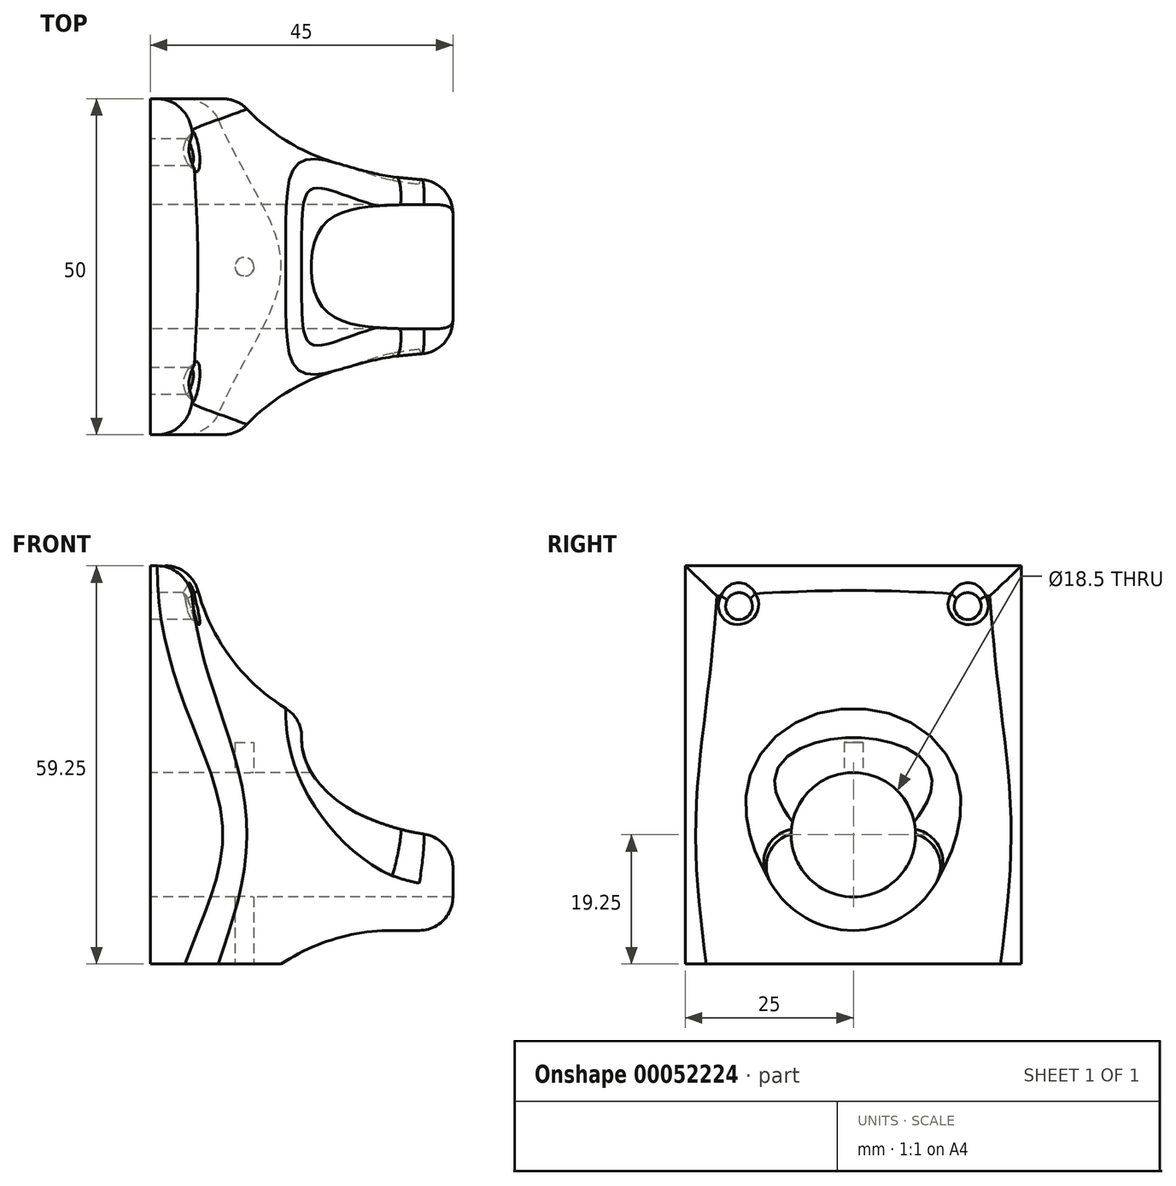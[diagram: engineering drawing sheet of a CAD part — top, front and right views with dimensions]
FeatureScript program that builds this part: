
annotation { "Feature Type Name" : "Feature", "Feature Type Description" : "" }
export const myFeature = defineFeature(function(context is Context, id is Id, definition is map)
    precondition{}
    {
        {
            var Q0;
            Q0=qCreatedBy(makeId("Right.planeOp"),FACE);
            var sketch = newSketch(context, id + "F0", { "sketchPlane" : qUnion([Q0])});
            skLineSegment(sketch, "E0.bottom", {"start": v(-25, 40) * mm, "end": v(25, 40) * mm});
            skLineSegment(sketch, "E0.top", {"start": v(-25, -19.25) * mm, "end": v(25, -19.25) * mm});
            skLineSegment(sketch, "E0.left", {"start": v(-25, 40) * mm, "end": v(-25, -19.25) * mm});
            skLineSegment(sketch, "E0.right", {"start": v(25, 40) * mm, "end": v(25, -19.25) * mm});
            skCircle(sketch, "E1", {"center": v(0, 0) * mm, "radius": 9.25 * mm});
            skCircle(sketch, "E2", {"center": v(0, 0) * mm, "radius": 14.25 * mm});
            skLineSegment(sketch, "E3", {"start": v(0, 40) * mm, "end": v(0, -19.25) * mm, "construction": true});
            skCircle(sketch, "E4", {"center": v(-17, 34) * mm, "radius": 2 * mm});
            skCircle(sketch, "E5.MirrorC", {"center": v(17, 34) * mm, "radius": 2 * mm});
            skSolve(sketch);
        }
        {
            var Q0;
            Q0=makeQuery(id+"F0.imprint","IMPRINT",FACE,{"disambiguationData":[TD([[makeQuery(id+"F0.imprint","IMPRINT",EDGE,{"derivedFrom":sQuery(id+"F0.wireOp",EDGE,"E0.bottom")}),-1.0]])]});
            var Q1;
            Q1=makeQuery(id+"F0.imprint","IMPRINT",FACE,{"disambiguationData":[TD([[makeQuery(id+"F0.imprint","IMPRINT",EDGE,{"derivedFrom":sQuery(id+"F0.wireOp",EDGE,"E1")}),-1.0]])]});
            extrude(context, id + "F1", {"entities" : qUnion([Q0, Q1]), "depth" : 6 * mm});
        }
        {
            var Q0;
            Q0=makeQuery(id+"F0.imprint","IMPRINT",FACE,{"disambiguationData":[TD([[makeQuery(id+"F0.imprint","IMPRINT",EDGE,{"derivedFrom":sQuery(id+"F0.wireOp",EDGE,"E1")}),-1.0]])]});
            extrude(context, id + "F2", {"entities" : qUnion([Q0]), "operationType" : NewBodyOperationType.ADD, "depth" : 45 * mm});
        }
        {
            var Q0;
            Q0=qCreatedBy(makeId("Front.planeOp"),FACE);
            var sketch = newSketch(context, id + "F3", { "sketchPlane" : qUnion([Q0])});
            skLineSegment(sketch, "E6.0", {"start": v(45, 14.25) * mm, "end": v(45, -14.25) * mm, "construction": true});
            skEllipse(sketch, "E7", {"center": v(45, 14.25) * mm, "majorRadius": 22.5 * mm, "minorRadius": 14.25 * mm, "majorAxis": v(-1, 0)});
            skLineSegment(sketch, "E8", {"start": v(45, 14.25) * mm, "end": v(0, 14.25) * mm, "construction": true});
            skLineSegment(sketch, "E9", {"start": v(0, 0) * mm, "end": v(45, 0) * mm, "construction": true});
            skLineSegment(sketch, "E10", {"start": v(22.5, 0) * mm, "end": v(22.5, 14.25) * mm, "construction": true});
            skSolve(sketch);
        }
        {
            var Q0;
            Q0 = qSketchRegion(id + "F3", true);
            extrude(context, id + "F4", {"entities" : qUnion([Q0]), "operationType" : NewBodyOperationType.REMOVE, "endBound" : BoundingType.THROUGH_ALL, "oppositeDirection" : true, "depth" : 25 * mm, "hasSecondDirection" : true, "secondDirectionBound" : SecondDirectionBoundingType.THROUGH_ALL, "secondDirectionOppositeDirection" : false, "secondDirectionDepth" : 25 * mm});
        }
        {
            var Q0;
            Q0=makeQuery(id+"F2.boolean.opBoolean","INTERSECT",EDGE,{"derivedFrom":[makeQuery(id+"F1.opExtrude","CAP_FACE",FACE,{"disambiguationData":[OSD([sQuery(id+"F0.wireOp",EDGE,"E0.bottom"),sQuery(id+"F0.wireOp",EDGE,"E0.top"),sQuery(id+"F0.wireOp",EDGE,"E0.left"),sQuery(id+"F0.wireOp",EDGE,"E0.right"),sQuery(id+"F0.wireOp",EDGE,"E1"),sQuery(id+"F0.wireOp",EDGE,"E4"),sQuery(id+"F0.wireOp",EDGE,"E5.MirrorC")])],"isStart":false}),makeQuery(id+"F2.opExtrude","SWEPT_FACE",FACE,{"disambiguationData":[OSD([sQuery(id+"F0.wireOp",EDGE,"E2")])]})]});
            fillet(context, id + "F5", {"entities" : qUnion([Q0]), "radius" : 30 * mm, "tangentPropagation" : true, "allowEdgeOverflow" : false});
        }
        {
            var Q0;
            {var subQ0=sQuery(id+"F0.wireOp",EDGE,"E0.right");Q0=makeQuery(id+"F5.opFillet","BLEND_EDGE",EDGE,{"blendedFrom":[makeQuery(id+"F2.boolean.opBoolean","INTERSECT",EDGE,{"derivedFrom":[makeQuery(id+"F1.opExtrude","CAP_FACE",FACE,{"disambiguationData":[OSD([sQuery(id+"F0.wireOp",EDGE,"E0.bottom"),sQuery(id+"F0.wireOp",EDGE,"E0.top"),sQuery(id+"F0.wireOp",EDGE,"E0.left"),subQ0,sQuery(id+"F0.wireOp",EDGE,"E1"),sQuery(id+"F0.wireOp",EDGE,"E4"),sQuery(id+"F0.wireOp",EDGE,"E5.MirrorC")])],"isStart":false}),makeQuery(id+"F2.opExtrude","SWEPT_FACE",FACE,{"disambiguationData":[OSD([sQuery(id+"F0.wireOp",EDGE,"E2")])]})]}),makeQuery(id+"F1.opExtrude","SWEPT_FACE",FACE,{"disambiguationData":[OSD([subQ0])]})],"blendedInto":[makeQuery(id+"F1.opExtrude","SWEPT_FACE",FACE,{"disambiguationData":[OSD([subQ0])]})]});}
            var Q1;
            {var subQ0=sQuery(id+"F0.wireOp",EDGE,"E0.bottom");Q1=makeQuery(id+"F5.opFillet","BLEND_EDGE",EDGE,{"blendedFrom":[makeQuery(id+"F2.boolean.opBoolean","INTERSECT",EDGE,{"derivedFrom":[makeQuery(id+"F1.opExtrude","CAP_FACE",FACE,{"disambiguationData":[OSD([subQ0,sQuery(id+"F0.wireOp",EDGE,"E0.top"),sQuery(id+"F0.wireOp",EDGE,"E0.left"),sQuery(id+"F0.wireOp",EDGE,"E0.right"),sQuery(id+"F0.wireOp",EDGE,"E1"),sQuery(id+"F0.wireOp",EDGE,"E4"),sQuery(id+"F0.wireOp",EDGE,"E5.MirrorC")])],"isStart":false}),makeQuery(id+"F2.opExtrude","SWEPT_FACE",FACE,{"disambiguationData":[OSD([sQuery(id+"F0.wireOp",EDGE,"E2")])]})]}),makeQuery(id+"F1.opExtrude","SWEPT_FACE",FACE,{"disambiguationData":[OSD([subQ0])]})],"blendedInto":[makeQuery(id+"F1.opExtrude","SWEPT_FACE",FACE,{"disambiguationData":[OSD([subQ0])]})]});}
            var Q2;
            {var subQ0=sQuery(id+"F0.wireOp",EDGE,"E0.left");Q2=makeQuery(id+"F5.opFillet","BLEND_EDGE",EDGE,{"blendedFrom":[makeQuery(id+"F2.boolean.opBoolean","INTERSECT",EDGE,{"derivedFrom":[makeQuery(id+"F1.opExtrude","CAP_FACE",FACE,{"disambiguationData":[OSD([sQuery(id+"F0.wireOp",EDGE,"E0.bottom"),sQuery(id+"F0.wireOp",EDGE,"E0.top"),subQ0,sQuery(id+"F0.wireOp",EDGE,"E0.right"),sQuery(id+"F0.wireOp",EDGE,"E1"),sQuery(id+"F0.wireOp",EDGE,"E4"),sQuery(id+"F0.wireOp",EDGE,"E5.MirrorC")])],"isStart":false}),makeQuery(id+"F2.opExtrude","SWEPT_FACE",FACE,{"disambiguationData":[OSD([sQuery(id+"F0.wireOp",EDGE,"E2")])]})]}),makeQuery(id+"F1.opExtrude","SWEPT_FACE",FACE,{"disambiguationData":[OSD([subQ0])]})],"blendedInto":[makeQuery(id+"F1.opExtrude","SWEPT_FACE",FACE,{"disambiguationData":[OSD([subQ0])]})]});}
            fillet(context, id + "F6", {"entities" : qUnion([Q0, Q1, Q2]), "radius" : 5 * mm, "tangentPropagation" : true, "allowEdgeOverflow" : false});
        }
        {
            var Q0;
            Q0=makeQuery(id+"F5.opFillet","BLEND_EDGE",EDGE,{"blendedFrom":[makeQuery(id+"F2.boolean.opBoolean","INTERSECT",EDGE,{"derivedFrom":[makeQuery(id+"F1.opExtrude","CAP_FACE",FACE,{"disambiguationData":[OSD([sQuery(id+"F0.wireOp",EDGE,"E0.bottom"),sQuery(id+"F0.wireOp",EDGE,"E0.top"),sQuery(id+"F0.wireOp",EDGE,"E0.left"),sQuery(id+"F0.wireOp",EDGE,"E0.right"),sQuery(id+"F0.wireOp",EDGE,"E1"),sQuery(id+"F0.wireOp",EDGE,"E4"),sQuery(id+"F0.wireOp",EDGE,"E5.MirrorC")])],"isStart":false}),makeQuery(id+"F2.opExtrude","SWEPT_FACE",FACE,{"disambiguationData":[OSD([sQuery(id+"F0.wireOp",EDGE,"E2")])]})]}),makeQuery(id+"F4.boolean.opBoolean","COPY",FACE,{"derivedFrom":makeQuery(id+"F4.opExtrude","SWEPT_FACE",FACE,{"disambiguationData":[OSD([sQuery(id+"F3.wireOp",EDGE,"E7")])]})})],"blendedInto":[makeQuery(id+"F4.boolean.opBoolean","COPY",FACE,{"derivedFrom":makeQuery(id+"F4.opExtrude","SWEPT_FACE",FACE,{"disambiguationData":[OSD([sQuery(id+"F3.wireOp",EDGE,"E7")])]})})]});
            fillet(context, id + "F7", {"entities" : qUnion([Q0]), "radius" : 5 * mm, "tangentPropagation" : true, "allowEdgeOverflow" : false});
        }
        {
            var Q0;
            Q0=makeQuery(id+"F2.opExtrude","CAP_EDGE",EDGE,{"disambiguationData":[OSD([sQuery(id+"F0.wireOp",EDGE,"E2")])],"isStart":false});
            fillet(context, id + "F8", {"entities" : qUnion([Q0]), "radius" : 5 * mm, "tangentPropagation" : true, "allowEdgeOverflow" : false});
        }
        {
            var Q0;
            {var subQ0=sQuery(id+"F0.wireOp",EDGE,"E5.MirrorC");Q0=makeQuery(id+"F5.opFillet","BLEND_EDGE",EDGE,{"blendedFrom":[makeQuery(id+"F2.boolean.opBoolean","INTERSECT",EDGE,{"derivedFrom":[makeQuery(id+"F1.opExtrude","CAP_FACE",FACE,{"disambiguationData":[OSD([sQuery(id+"F0.wireOp",EDGE,"E0.bottom"),sQuery(id+"F0.wireOp",EDGE,"E0.top"),sQuery(id+"F0.wireOp",EDGE,"E0.left"),sQuery(id+"F0.wireOp",EDGE,"E0.right"),sQuery(id+"F0.wireOp",EDGE,"E1"),sQuery(id+"F0.wireOp",EDGE,"E4"),subQ0])],"isStart":false}),makeQuery(id+"F2.opExtrude","SWEPT_FACE",FACE,{"disambiguationData":[OSD([sQuery(id+"F0.wireOp",EDGE,"E2")])]})]}),makeQuery(id+"F1.opExtrude","SWEPT_FACE",FACE,{"disambiguationData":[OSD([subQ0])]})],"blendedInto":[makeQuery(id+"F1.opExtrude","SWEPT_FACE",FACE,{"disambiguationData":[OSD([subQ0])]})]});}
            var Q1;
            {var subQ0=sQuery(id+"F0.wireOp",EDGE,"E4");Q1=makeQuery(id+"F5.opFillet","BLEND_EDGE",EDGE,{"blendedFrom":[makeQuery(id+"F2.boolean.opBoolean","INTERSECT",EDGE,{"derivedFrom":[makeQuery(id+"F1.opExtrude","CAP_FACE",FACE,{"disambiguationData":[OSD([sQuery(id+"F0.wireOp",EDGE,"E0.bottom"),sQuery(id+"F0.wireOp",EDGE,"E0.top"),sQuery(id+"F0.wireOp",EDGE,"E0.left"),sQuery(id+"F0.wireOp",EDGE,"E0.right"),sQuery(id+"F0.wireOp",EDGE,"E1"),subQ0,sQuery(id+"F0.wireOp",EDGE,"E5.MirrorC")])],"isStart":false}),makeQuery(id+"F2.opExtrude","SWEPT_FACE",FACE,{"disambiguationData":[OSD([sQuery(id+"F0.wireOp",EDGE,"E2")])]})]}),makeQuery(id+"F1.opExtrude","SWEPT_FACE",FACE,{"disambiguationData":[OSD([subQ0])]})],"blendedInto":[makeQuery(id+"F1.opExtrude","SWEPT_FACE",FACE,{"disambiguationData":[OSD([subQ0])]})]});}
            chamfer(context, id + "F9", {"entities" : qUnion([Q0, Q1]), "width" : 1 * mm, "tangentPropagation" : true});
        }
        {
            var Q0;
            Q0=makeQuery(id+"F1.opExtrude","SWEPT_FACE",FACE,{"disambiguationData":[OSD([sQuery(id+"F0.wireOp",EDGE,"E0.top")])]});
            var sketch = newSketch(context, id + "F10", { "sketchPlane" : qUnion([Q0])});
            skLineSegment(sketch, "E11", {"start": v(0, 0) * mm, "end": v(45.25, 0) * mm, "construction": true});
            skPoint(sketch, "E11.endSnap0", {"position": v(0, 0) * mm});
            skCircle(sketch, "E12", {"center": v(14, 0) * mm, "radius": 1.4 * mm});
            skSolve(sketch);
        }
        {
            var Q0;
            Q0=makeQuery(id+"F10.imprint","IMPRINT",FACE,{"disambiguationData":[TD([[makeQuery(id+"F10.imprint","IMPRINT",EDGE,{"derivedFrom":sQuery(id+"F10.wireOp",EDGE,"E12")}),1.0]])]});
            extrude(context, id + "F11", {"entities" : qUnion([Q0]), "operationType" : NewBodyOperationType.REMOVE, "oppositeDirection" : true, "depth" : 33 * mm});
        }
    });
